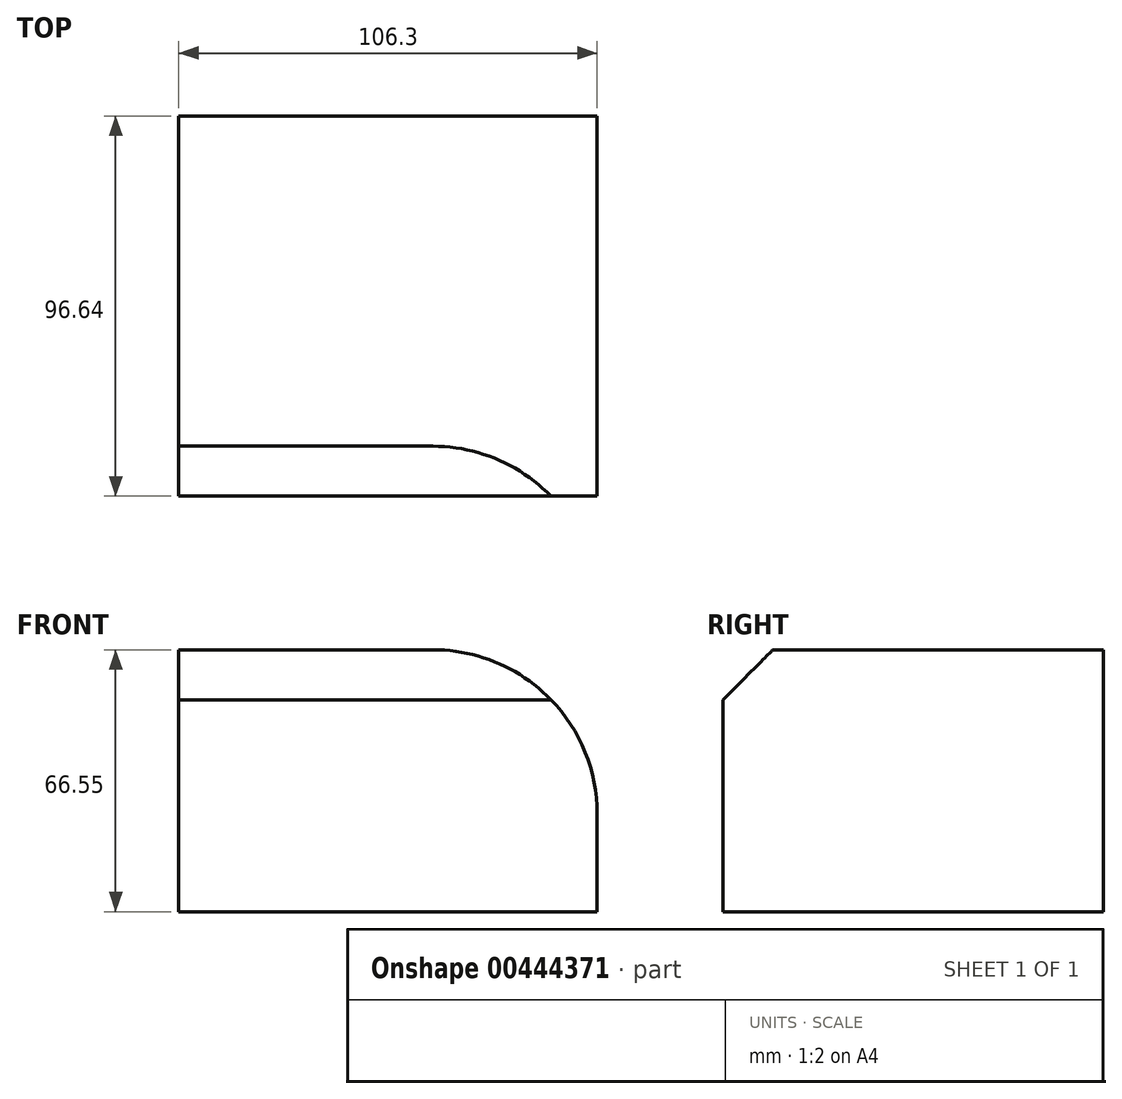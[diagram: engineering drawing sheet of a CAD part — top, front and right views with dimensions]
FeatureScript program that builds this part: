
annotation { "Feature Type Name" : "Feature", "Feature Type Description" : "" }
export const myFeature = defineFeature(function(context is Context, id is Id, definition is map)
    precondition{}
    {
        {
            var Q0;
            Q0=qCreatedBy(makeId("Top.planeOp"),FACE);
            var sketch = newSketch(context, id + "F0", { "sketchPlane" : qUnion([Q0])});
            skLineSegment(sketch, "E0.bottom", {"start": v(-52.7, -51.45) * mm, "end": v(53.6, -51.45) * mm});
            skLineSegment(sketch, "E0.top", {"start": v(-52.7, 45.2) * mm, "end": v(53.6, 45.2) * mm});
            skLineSegment(sketch, "E0.left", {"start": v(-52.7, -51.45) * mm, "end": v(-52.7, 45.2) * mm});
            skLineSegment(sketch, "E0.right", {"start": v(53.6, -51.45) * mm, "end": v(53.6, 45.2) * mm});
            skSolve(sketch);
        }
        {
            var Q0;
            Q0 = qSketchRegion(id + "F0", true);
            extrude(context, id + "F1", {"entities" : qUnion([Q0]), "depth" : 66.55 * mm});
        }
        {
            var Q0;
            Q0=makeQuery(id+"F1.opExtrude","CAP_EDGE",EDGE,{"disambiguationData":[OSD([sQuery(id+"F0.wireOp",EDGE,"E0.bottom")])],"isStart":false});
            chamfer(context, id + "F2", {"entities" : qUnion([Q0]), "width" : 12.7 * mm, "tangentPropagation" : true});
        }
        {
            var Q0;
            Q0=makeQuery(id+"F1.opExtrude","CAP_EDGE",EDGE,{"disambiguationData":[OSD([sQuery(id+"F0.wireOp",EDGE,"E0.right")])],"isStart":false});
            fillet(context, id + "F3", {"entities" : qUnion([Q0]), "radius" : 41.7 * mm, "tangentPropagation" : true, "allowEdgeOverflow" : false});
        }
    });
